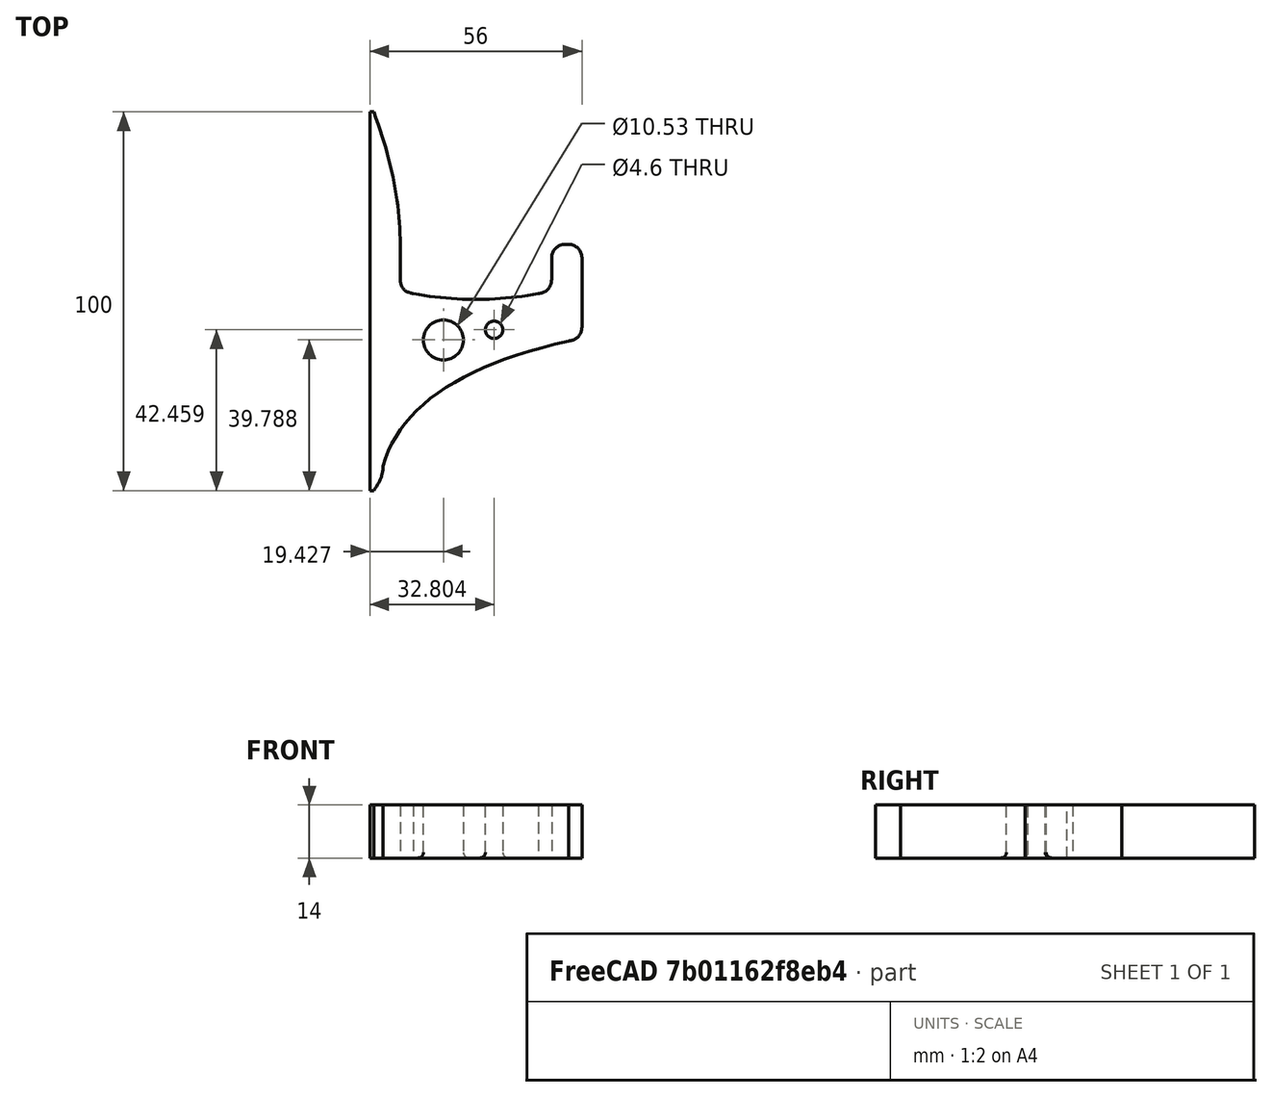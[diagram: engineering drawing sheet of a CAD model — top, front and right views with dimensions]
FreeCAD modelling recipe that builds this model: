
FCSTD DOCUMENT  (FreeCAD 0.19R0.19.2)
Label: headphoneStandWithHookStudsRemovedCurrent_4
License: All rights reserved
LicenseURL: http://en.wikipedia.org/wiki/All_rights_reserved
objects: Part::Fillet×2, Sketcher::SketchObject×1, Part::Extrusion×1, Part::Mirroring×1
note: 5 computed .brp shape members not serialized (recipe doc carries the construction recipe); baked Part::Feature solids carry a one-line shape summary decoded from their .brp

FEATURE [Sketcher::SketchObject] Sketch
  FullyConstrained = false
  sketch-geometry (51):
    g0: LineSegment StartX=0 StartY=0 StartZ=0 EndX=0 EndY=100 EndZ=0
    g1: LineSegment StartX=8 StartY=65 StartZ=0 EndX=8 EndY=56 EndZ=0
    g2: Circle CenterX=8 CenterY=56 CenterZ=0 NormalX=0 NormalY=0 NormalZ=1 AngleXU=0 Radius=1
    g3: Circle CenterX=8 CenterY=52.5 CenterZ=0 NormalX=0 NormalY=0 NormalZ=1 AngleXU=0 Radius=1
    g4: Circle CenterX=11.5 CenterY=52 CenterZ=0 NormalX=0 NormalY=0 NormalZ=1 AngleXU=0 Radius=1
    g5: BSplineCurve PolesCount=3 KnotsCount=2 Degree=2 IsPeriodic=0
    g6: GeomPoint X=8 Y=56 Z=0
    g7: GeomPoint X=11.5 Y=52 Z=0
    g8: Circle CenterX=44.5 CenterY=52 CenterZ=0 NormalX=0 NormalY=0 NormalZ=1 AngleXU=0 Radius=1
    g9: Circle CenterX=48 CenterY=52.5 CenterZ=0 NormalX=0 NormalY=0 NormalZ=1 AngleXU=0 Radius=1
    g10: Circle CenterX=48 CenterY=56 CenterZ=0 NormalX=0 NormalY=0 NormalZ=1 AngleXU=0 Radius=1
    g11: BSplineCurve PolesCount=3 KnotsCount=2 Degree=2 IsPeriodic=0
    g12: GeomPoint X=44.5 Y=52 Z=0
    g13: GeomPoint X=48 Y=56 Z=0
    g14: Circle CenterX=11.5 CenterY=52 CenterZ=0 NormalX=0 NormalY=0 NormalZ=1 AngleXU=0 Radius=1
    g15: Circle CenterX=28 CenterY=49 CenterZ=0 NormalX=0 NormalY=0 NormalZ=1 AngleXU=0 Radius=1
    g16: Circle CenterX=44.5 CenterY=52 CenterZ=0 NormalX=0 NormalY=0 NormalZ=1 AngleXU=0 Radius=1
    g17: BSplineCurve PolesCount=3 KnotsCount=2 Degree=2 IsPeriodic=0
    g18: GeomPoint X=11.5 Y=52 Z=0
    g19: GeomPoint X=44.5 Y=52 Z=0
    g20: LineSegment StartX=48 StartY=65 StartZ=0 EndX=48 EndY=56 EndZ=0
    g21: LineSegment StartX=48 StartY=65 StartZ=0 EndX=56 EndY=65 EndZ=0
    g22: LineSegment StartX=56 StartY=65 StartZ=0 EndX=56 EndY=43.5 EndZ=0
    g23: Circle CenterX=56 CenterY=43.5 CenterZ=0 NormalX=0 NormalY=0 NormalZ=1 AngleXU=0 Radius=1
    g24: Circle CenterX=56 CenterY=40 CenterZ=0 NormalX=0 NormalY=0 NormalZ=1 AngleXU=0 Radius=1
    g25: Circle CenterX=52.5 CenterY=39.5 CenterZ=0 NormalX=0 NormalY=0 NormalZ=1 AngleXU=0 Radius=1
    g26: BSplineCurve PolesCount=3 KnotsCount=2 Degree=2 IsPeriodic=0
    g27: GeomPoint X=56 Y=43.5 Z=0
    g28: GeomPoint X=52.5 Y=39.5 Z=0
    g29: LineSegment StartX=0 StartY=0 StartZ=0 EndX=1 EndY=0 EndZ=0
    g30: LineSegment StartX=0 StartY=100 StartZ=0 EndX=1 EndY=100 EndZ=0
    g31: Circle CenterX=8 CenterY=65 CenterZ=0 NormalX=0 NormalY=0 NormalZ=1 AngleXU=0 Radius=1
    g32: Circle CenterX=8 CenterY=81.5 CenterZ=0 NormalX=0 NormalY=0 NormalZ=1 AngleXU=0 Radius=1
    g33: Circle CenterX=1 CenterY=100 CenterZ=0 NormalX=0 NormalY=0 NormalZ=1 AngleXU=0 Radius=1
    g34: BSplineCurve PolesCount=3 KnotsCount=2 Degree=2 IsPeriodic=0
    g35: GeomPoint X=8 Y=65 Z=0
    g36: GeomPoint X=1 Y=100 Z=0
    g37: Circle CenterX=1 CenterY=0 CenterZ=0 NormalX=0 NormalY=0 NormalZ=1 AngleXU=0 Radius=1
    g38: Circle CenterX=3.5 CenterY=3.3 CenterZ=0 NormalX=0 NormalY=0 NormalZ=1 AngleXU=0 Radius=1
    g39: Circle CenterX=3.5 CenterY=6.5 CenterZ=0 NormalX=0 NormalY=0 NormalZ=1 AngleXU=0 Radius=1
    g40: BSplineCurve PolesCount=3 KnotsCount=2 Degree=2 IsPeriodic=0
    g41: GeomPoint X=1 Y=0 Z=0
    g42: GeomPoint X=3.5 Y=6.5 Z=0
    g43: Circle CenterX=52.5 CenterY=39.5 CenterZ=0 NormalX=0 NormalY=0 NormalZ=1 AngleXU=0 Radius=1
    g44: Circle CenterX=10 CenterY=30 CenterZ=0 NormalX=0 NormalY=0 NormalZ=1 AngleXU=0 Radius=1
    g45: Circle CenterX=3.5 CenterY=6.5 CenterZ=0 NormalX=0 NormalY=0 NormalZ=1 AngleXU=0 Radius=1
    g46: BSplineCurve PolesCount=3 KnotsCount=2 Degree=2 IsPeriodic=0
    g47: GeomPoint X=52.5 Y=39.5 Z=0
    g48: GeomPoint X=3.5 Y=6.5 Z=0
    g49: Circle CenterX=19.4268 CenterY=39.7877 CenterZ=0 NormalX=0 NormalY=0 NormalZ=1 AngleXU=0 Radius=5.26565
    g50: Circle CenterX=32.8037 CenterY=42.4589 CenterZ=0 NormalX=0 NormalY=0 NormalZ=1 AngleXU=0 Radius=2.29927
  constraints (92):
    c: Vertical(g0)
    c: Distance(g0) = 100
    c: Coincident(g0,g-1)
    c: Block(g0)
    c: Vertical(g1)
    c: Distance(g1) = 9
    c: Block(g1)
    c: Weight(g2) = 1
    c: Equal(g2,g3)
    c: Equal(g2,g4)
    c: InternalAlignment(g2,g5)
    c: InternalAlignment(g3,g5)
    c: InternalAlignment(g4,g5)
    c: InternalAlignment(g6,g5)
    c: InternalAlignment(g7,g5)
    c: Coincident(g5,g1)
    c: Block(g5)
    c: Weight(g8) = 1
    c: Equal(g8,g9)
    c: Equal(g8,g10)
    c: InternalAlignment(g8,g11)
    c: InternalAlignment(g9,g11)
    c: InternalAlignment(g10,g11)
    c: InternalAlignment(g12,g11)
    c: InternalAlignment(g13,g11)
    c: Block(g11)
    c: Weight(g14) = 1
    c: Equal(g14,g15)
    c: Equal(g14,g16)
    c: InternalAlignment(g14,g17)
    c: InternalAlignment(g15,g17)
    c: InternalAlignment(g16,g17)
    c: InternalAlignment(g18,g17)
    c: InternalAlignment(g19,g17)
    c: Coincident(g17,g5)
    c: Coincident(g17,g11)
    c: Block(g17)
    c: Vertical(g20)
    c: Coincident(g20,g11)
    c: Equal(g1,g20)
    c: Horizontal(g21)
    c: Coincident(g21,g20)
    c: Distance(g21) = 8
    c: Vertical(g22)
    c: Block(g21)
    c: Coincident(g22,g21)
    c: Distance(g22) = 21.5
    c: Weight(g23) = 1
    c: Equal(g23,g24)
    c: Equal(g23,g25)
    c: InternalAlignment(g23,g26)
    c: InternalAlignment(g24,g26)
    c: InternalAlignment(g25,g26)
    c: InternalAlignment(g27,g26)
    c: InternalAlignment(g28,g26)
    c: Coincident(g26,g22)
    c: Block(g26)
    c: Horizontal(g29)
    c: Distance(g29) = 1
    c: Coincident(g29,g0)
    c: Block(g29)
    c: Horizontal(g30)
    c: Distance(g30) = 1
    c: Coincident(g30,g0)
    c: Block(g30)
    c: Weight(g31) = 1
    c: Equal(g31,g32)
    c: Equal(g31,g33)
    c: InternalAlignment(g31,g34)
    c: InternalAlignment(g32,g34)
    c: InternalAlignment(g33,g34)
    c: InternalAlignment(g35,g34)
    c: InternalAlignment(g36,g34)
    c: Coincident(g34,g30)
    c: Coincident(g34,g1)
    c: Block(g34)
    c: Weight(g37) = 1
    c: Equal(g37,g38)
    c: Equal(g37,g39)
    c: InternalAlignment(g37,g40)
    c: InternalAlignment(g38,g40)
    c: InternalAlignment(g39,g40)
    c: InternalAlignment(g41,g40)
    c: InternalAlignment(g44,g46)
    c: InternalAlignment(g45,g46)
    c: InternalAlignment(g47,g46)
    c: InternalAlignment(g48,g46)
    c: Coincident(g46,g40)
    c: Coincident(g46,g26)
    c: Block(g46)
    c: Block(g49)
    c: Block(g50)
FEATURE [Part::Extrusion] Extrude
  Base = -> Sketch
  Dir = (0,0,1)
  DirMode = 2
  FaceMakerClass = Part::FaceMakerBullseye
  LengthFwd = 14
  LengthRev = 0
  Solid = true
  Symmetric = false
FEATURE [Part::Fillet] Fillet
  Base = -> Extrude
  Edges = 2 edges r=3.5: [Edge26,Edge29]
FEATURE [Part::Fillet] Fillet001
  Base = -> Fillet
  Edges = 2 edges r=1.5: [Edge39,Edge40]
FEATURE [Part::Mirroring] Part__Mirroring  label="Fillet001 (Mirror #1)"
  Base = (0,0,0)
  Normal = (0,0,1)
  Source = -> Fillet001
